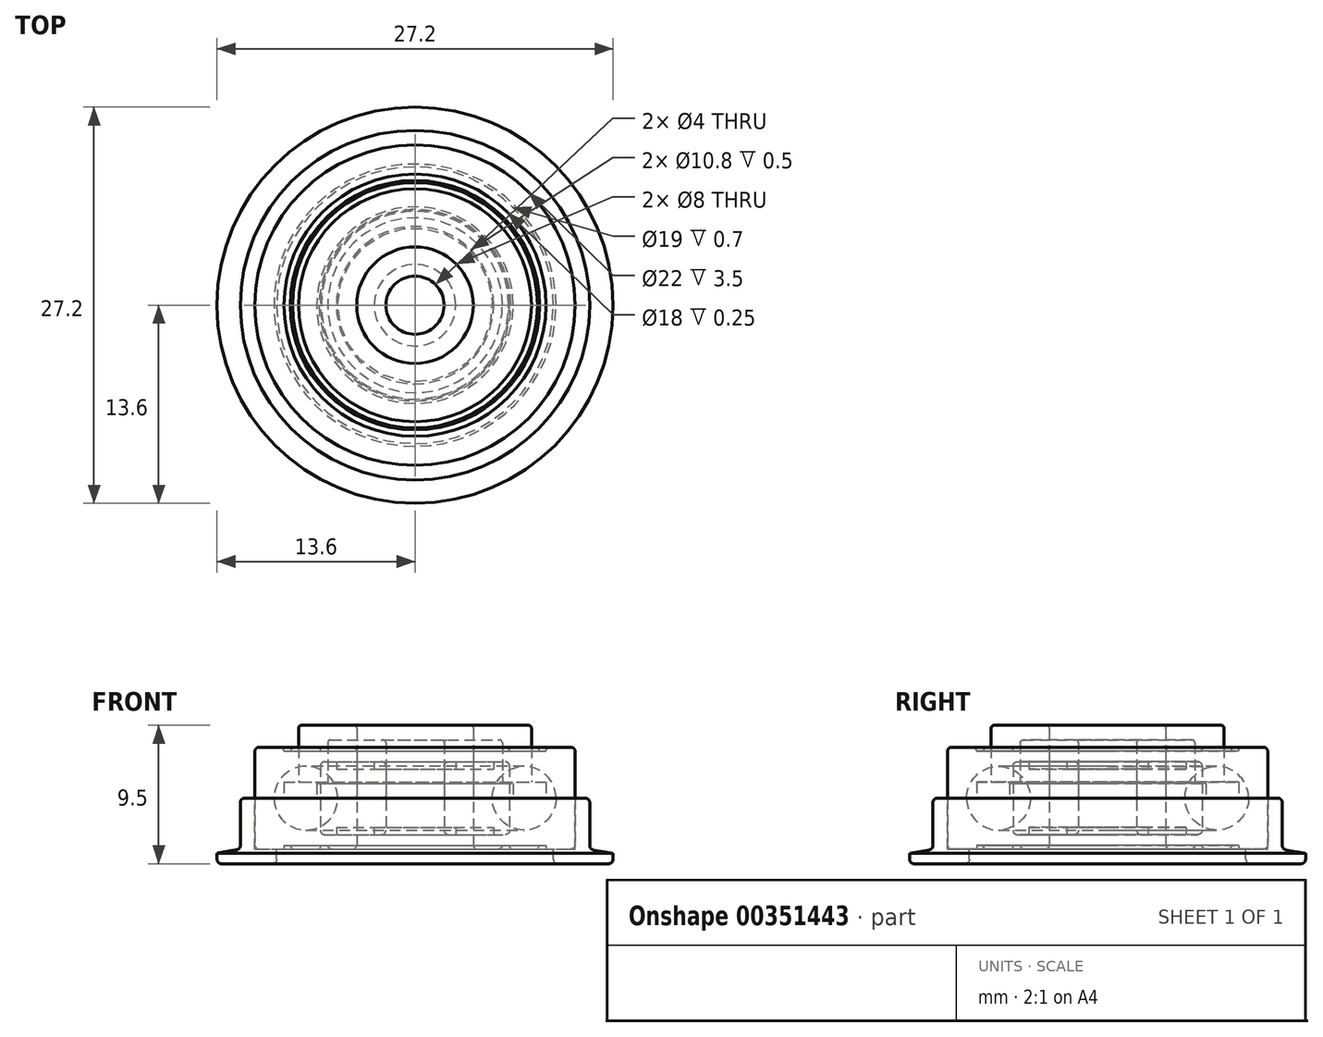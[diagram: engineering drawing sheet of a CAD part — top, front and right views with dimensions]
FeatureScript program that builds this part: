
annotation { "Feature Type Name" : "Feature", "Feature Type Description" : "" }
export const myFeature = defineFeature(function(context is Context, id is Id, definition is map)
    precondition{}
    {
        {
            var Q0;
            Q0=qCreatedBy(makeId("Front.planeOp"),FACE);
            var sketch = newSketch(context, id + "F0", { "sketchPlane" : qUnion([Q0])});
            skLineSegment(sketch, "E0", {"start": v(0, 0) * mm, "end": v(4, 0) * mm, "construction": true});
            skLineSegment(sketch, "E1", {"start": v(4, 0) * mm, "end": v(4, -3.5) * mm});
            skLineSegment(sketch, "E2", {"start": v(4, -3.5) * mm, "end": v(6, -3.5) * mm});
            skLineSegment(sketch, "E3", {"start": v(6, -3.5) * mm, "end": v(6, -3.25) * mm});
            skLineSegment(sketch, "E4", {"start": v(6, -3.25) * mm, "end": v(6.44, -3.25) * mm});
            skLineSegment(sketch, "E5", {"start": v(6.44, -3.25) * mm, "end": v(6.58, -3.5) * mm});
            skLineSegment(sketch, "E6", {"start": v(6.58, -3.5) * mm, "end": v(8.42, -3.5) * mm});
            skLineSegment(sketch, "E7", {"start": v(8.42, -3.5) * mm, "end": v(8.56, -3.25) * mm});
            skLineSegment(sketch, "E8", {"start": v(8.56, -3.25) * mm, "end": v(9, -3.25) * mm});
            skLineSegment(sketch, "E9", {"start": v(9, -3.25) * mm, "end": v(9, -3.5) * mm});
            skLineSegment(sketch, "E10", {"start": v(9, -3.5) * mm, "end": v(11, -3.5) * mm});
            skLineSegment(sketch, "E11", {"start": v(11, -3.5) * mm, "end": v(11, 0) * mm});
            skLineSegment(sketch, "E12.0.MirrorCS", {"start": v(4, 3.5) * mm, "end": v(6, 3.5) * mm});
            skLineSegment(sketch, "E12.1.MirrorCS", {"start": v(11, 3.5) * mm, "end": v(11, 0) * mm});
            skLineSegment(sketch, "E12.2.MirrorCS", {"start": v(4, 0) * mm, "end": v(4, 3.5) * mm});
            skLineSegment(sketch, "E12.3.MirrorCS", {"start": v(6, 3.25) * mm, "end": v(6.44, 3.25) * mm});
            skLineSegment(sketch, "E12.4.MirrorCS", {"start": v(9, 3.25) * mm, "end": v(9, 3.5) * mm});
            skLineSegment(sketch, "E12.5.MirrorCS", {"start": v(6.44, 3.25) * mm, "end": v(6.58, 3.5) * mm});
            skLineSegment(sketch, "E12.6.MirrorCS", {"start": v(6.58, 3.5) * mm, "end": v(8.42, 3.5) * mm});
            skLineSegment(sketch, "E12.7.MirrorCS", {"start": v(8.42, 3.5) * mm, "end": v(8.56, 3.25) * mm});
            skLineSegment(sketch, "E12.8.MirrorCS", {"start": v(9, 3.5) * mm, "end": v(11, 3.5) * mm});
            skLineSegment(sketch, "E12.9.MirrorCS", {"start": v(6, 3.5) * mm, "end": v(6, 3.25) * mm});
            skLineSegment(sketch, "E12.10.MirrorCS", {"start": v(8.56, 3.25) * mm, "end": v(9, 3.25) * mm});
            skLineSegment(sketch, "E13", {"start": v(0, 0) * mm, "end": v(0, 5.44) * mm, "construction": true});
            skLineSegment(sketch, "E14", {"start": v(0, 0) * mm, "end": v(-4, 0) * mm, "construction": true});
            skLineSegment(sketch, "E15", {"start": v(4, 0) * mm, "end": v(11, 0) * mm, "construction": true});
            skLineSegment(sketch, "E16", {"start": v(-4, 0) * mm, "end": v(-11, 0) * mm, "construction": true});
            skCircle(sketch, "E17", {"center": v(7.5, 0) * mm, "radius": 2.19 * mm});
            skSolve(sketch);
        }
        {
            var Q0;
            Q0=makeQuery(id+"F0.imprint","IMPRINT",FACE,{"disambiguationData":[TD([[makeQuery(id+"F0.imprint","IMPRINT",EDGE,{"derivedFrom":sQuery(id+"F0.wireOp",EDGE,"E2")}),1.0]])]});
            var Q1;
            Q1=sQuery(id+"F0.wireOp",EDGE,"E13");
            revolve(context, id + "F1", {"entities" : qUnion([Q0]), "axis" : qUnion([Q1]), "revolveType" : RevolveType.FULL});
        }
        {
            var Q0;
            Q0=qCreatedBy(makeId("Front.planeOp"),FACE);
            var sketch = newSketch(context, id + "F2", { "sketchPlane" : qUnion([Q0])});
            skLineSegment(sketch, "E18", {"start": v(0, 0) * mm, "end": v(0, 3.82) * mm, "construction": true});
            skLineSegment(sketch, "E19", {"start": v(0, 0) * mm, "end": v(2, 0) * mm, "construction": true});
            skLineSegment(sketch, "E20.0.MirrorCS", {"start": v(0, 0) * mm, "end": v(-2, 0) * mm, "construction": true});
            skLineSegment(sketch, "E21", {"start": v(0, 0) * mm, "end": v(6.5, 0) * mm, "construction": true});
            skLineSegment(sketch, "E22.0.MirrorCS", {"start": v(0, 0) * mm, "end": v(-6.5, 0) * mm, "construction": true});
            skLineSegment(sketch, "E23", {"start": v(6.5, 0) * mm, "end": v(6.5, 2.5) * mm});
            skLineSegment(sketch, "E24", {"start": v(2, 0) * mm, "end": v(2, 2.5) * mm});
            skLineSegment(sketch, "E25", {"start": v(2, 2.5) * mm, "end": v(2.8, 2.5) * mm});
            skLineSegment(sketch, "E26", {"start": v(2.8, 2.5) * mm, "end": v(2.8, 2) * mm});
            skLineSegment(sketch, "E27", {"start": v(2.8, 2) * mm, "end": v(5.4, 2) * mm});
            skLineSegment(sketch, "E28", {"start": v(5.4, 2) * mm, "end": v(5.4, 2.5) * mm});
            skLineSegment(sketch, "E29", {"start": v(5.4, 2.5) * mm, "end": v(6.5, 2.5) * mm});
            skLineSegment(sketch, "E30.0.MirrorCS", {"start": v(2, 0) * mm, "end": v(2, -2.5) * mm});
            skLineSegment(sketch, "E31.0.MirrorCS", {"start": v(2, -2.5) * mm, "end": v(2.8, -2.5) * mm});
            skLineSegment(sketch, "E32.0.MirrorCS", {"start": v(2.8, -2.5) * mm, "end": v(2.8, -2) * mm});
            skLineSegment(sketch, "E33.0.MirrorCS", {"start": v(2.8, -2) * mm, "end": v(5.4, -2) * mm});
            skLineSegment(sketch, "E34.0.MirrorCS", {"start": v(5.4, -2) * mm, "end": v(5.4, -2.5) * mm});
            skLineSegment(sketch, "E35.0.MirrorCS", {"start": v(5.4, -2.5) * mm, "end": v(6.5, -2.5) * mm});
            skLineSegment(sketch, "E36.0.MirrorCS", {"start": v(6.5, 0) * mm, "end": v(6.5, -2.5) * mm});
            skSolve(sketch);
        }
        {
            var Q0;
            Q0=makeQuery(id+"F2.imprint","IMPRINT",FACE,{"disambiguationData":[TD([[makeQuery(id+"F2.imprint","IMPRINT",EDGE,{"derivedFrom":sQuery(id+"F2.wireOp",EDGE,"E23")}),1.0]])]});
            var Q1;
            Q1=sQuery(id+"F2.wireOp",EDGE,"E18");
            revolve(context, id + "F3", {"entities" : qUnion([Q0]), "axis" : qUnion([Q1]), "revolveType" : RevolveType.FULL});
        }
        {
            var Q0;
            Q0=qCreatedBy(makeId("Front.planeOp"),FACE);
            var sketch = newSketch(context, id + "F4", { "sketchPlane" : qUnion([Q0])});
            skLineSegment(sketch, "E37.1", {"start": v(11, 3.5) * mm, "end": v(11, 0) * mm, "construction": true});
            skLineSegment(sketch, "E38.0", {"start": v(12, 3.5) * mm, "end": v(12, 0) * mm});
            skLineSegment(sketch, "E39", {"start": v(11, 0) * mm, "end": v(12, 0) * mm});
            skLineSegment(sketch, "E40", {"start": v(9.5, 4.5) * mm, "end": v(13.6, 4.5) * mm});
            skLineSegment(sketch, "E41", {"start": v(13.6, 4.5) * mm, "end": v(13.6, 3.78) * mm});
            skLineSegment(sketch, "E42", {"start": v(12, 3.5) * mm, "end": v(13.6, 3.78) * mm});
            skLineSegment(sketch, "E43", {"start": v(11, 3.5) * mm, "end": v(11, 0) * mm});
            skLineSegment(sketch, "E44.trimOffspring", {"start": v(9.5, 3.5) * mm, "end": v(11, 3.5) * mm});
            skLineSegment(sketch, "E45.0", {"start": v(4, 0) * mm, "end": v(4, 3.5) * mm, "construction": true});
            skLineSegment(sketch, "E46", {"start": v(9.5, 4.5) * mm, "end": v(9.5, 3.5) * mm});
            skSolve(sketch);
        }
        {
            var Q0;
            Q0=makeQuery(id+"F4.imprint","IMPRINT",FACE,{"disambiguationData":[TD([[makeQuery(id+"F4.imprint","IMPRINT",EDGE,{"derivedFrom":sQuery(id+"F4.wireOp",EDGE,"E38.0")}),-1.0]])]});
            var Q1;
            Q1=sQuery(id+"F0.wireOp",EDGE,"E13");
            revolve(context, id + "F5", {"entities" : qUnion([Q0]), "axis" : qUnion([Q1]), "revolveType" : RevolveType.FULL});
        }
        {
            var Q0;
            Q0=makeQuery(id+"F1.opRevolve","SWEPT_EDGE",EDGE,{"disambiguationData":[OSD([sQuery(id+"F0.wireOp",EDGE,"E11"),sQuery(id+"F0.wireOp",EDGE,"E12.8.MirrorCS")])]});
            var Q1;
            Q1=makeQuery(id+"F1.opRevolve","SWEPT_EDGE",EDGE,{"disambiguationData":[OSD([sQuery(id+"F0.wireOp",EDGE,"E12.0.MirrorCS"),sQuery(id+"F0.wireOp",EDGE,"E12.2.MirrorCS")])]});
            var Q2;
            Q2=makeQuery(id+"F1.opRevolve","SWEPT_EDGE",EDGE,{"disambiguationData":[OSD([sQuery(id+"F0.wireOp",EDGE,"E10"),sQuery(id+"F0.wireOp",EDGE,"E11")])]});
            var Q3;
            Q3=makeQuery(id+"F1.opRevolve","SWEPT_EDGE",EDGE,{"disambiguationData":[OSD([sQuery(id+"F0.wireOp",EDGE,"E2"),sQuery(id+"F0.wireOp",EDGE,"E12.2.MirrorCS")])]});
            var Q4;
            Q4=makeQuery(id+"F3.opRevolve","SWEPT_FACE",FACE,{"disambiguationData":[OSD([sQuery(id+"F2.wireOp",EDGE,"E23"),sQuery(id+"F2.wireOp",EDGE,"E36.0.MirrorCS")])]});
            var Q5;
            Q5=makeQuery(id+"F3.opRevolve","SWEPT_FACE",FACE,{"disambiguationData":[OSD([sQuery(id+"F2.wireOp",EDGE,"E24"),sQuery(id+"F2.wireOp",EDGE,"E30.0.MirrorCS")])]});
            var Q6;
            Q6=makeQuery(id+"F5.opRevolve","SWEPT_EDGE",EDGE,{"disambiguationData":[OSD([sQuery(id+"F4.wireOp",EDGE,"E38.0"),sQuery(id+"F4.wireOp",EDGE,"6174cbda-ea30-4576-b442-45a5408af237")])]});
            var Q7;
            Q7=makeQuery(id+"F5.opRevolve","SWEPT_EDGE",EDGE,{"disambiguationData":[OSD([sQuery(id+"F4.wireOp",EDGE,"E40"),sQuery(id+"F4.wireOp",EDGE,"E41")])]});
            var Q8;
            Q8=makeQuery(id+"F5.opRevolve","SWEPT_EDGE",EDGE,{"disambiguationData":[OSD([sQuery(id+"F4.wireOp",EDGE,"b3527501-35f9-4002-87d1-32b6eb9845c8.0"),sQuery(id+"F4.wireOp",EDGE,"E40")])]});
            fillet(context, id + "F6", {"entities" : qUnion([Q0, Q1, Q2, Q3, Q4, Q5, Q6, Q7, Q8]), "radius" : .3 * mm, "tangentPropagation" : true, "allowEdgeOverflow" : false});
        }
        {
            var Q0;
            Q0=makeQuery(id+"F5.opRevolve","SWEPT_BODY",BODY,{"disambiguationData":[OSD([sQuery(id+"F4.wireOp",EDGE,"E38.0"),sQuery(id+"F4.wireOp",EDGE,"E39"),sQuery(id+"F4.wireOp",EDGE,"E40"),sQuery(id+"F4.wireOp",EDGE,"E41"),sQuery(id+"F4.wireOp",EDGE,"E42"),sQuery(id+"F4.wireOp",EDGE,"E43"),sQuery(id+"F4.wireOp",EDGE,"E44.trimOffspring"),sQuery(id+"F4.wireOp",EDGE,"E46")])]});
            var Q1;
            Q1=sQuery(id+"F0.wireOp",EDGE,"E0");
            transform(context, id + "F7", {"entities" : qUnion([Q0]), "transformType" : TransformType.ROTATION, "transformAxis" : qUnion([Q1]), "angle" : 180 * degree, "makeCopy" : false});
        }
        {
            var Q0;
            Q0=qCreatedBy(makeId("Front.planeOp"),FACE);
            var sketch = newSketch(context, id + "F8", { "sketchPlane" : qUnion([Q0])});
            skLineSegment(sketch, "E47", {"start": v(0, 0) * mm, "end": v(0, 5) * mm, "construction": true});
            skLineSegment(sketch, "E48", {"start": v(4, 0) * mm, "end": v(4, 5) * mm});
            skLineSegment(sketch, "E49", {"start": v(4, 5) * mm, "end": v(8, 5) * mm});
            skLineSegment(sketch, "E50", {"start": v(8, 5) * mm, "end": v(8, 1.1) * mm});
            skLineSegment(sketch, "E51", {"start": v(8, 1.1) * mm, "end": v(9, 1.1) * mm});
            skLineSegment(sketch, "E52", {"start": v(9, 1.1) * mm, "end": v(9, 0) * mm});
            skLineSegment(sketch, "E53", {"start": v(9, 0) * mm, "end": v(4, 0) * mm});
            skSolve(sketch);
        }
        {
            var Q0;
            Q0=makeQuery(id+"F8.imprint","IMPRINT",FACE,{"disambiguationData":[TD([[makeQuery(id+"F8.imprint","IMPRINT",EDGE,{"derivedFrom":sQuery(id+"F8.wireOp",EDGE,"E48")}),-1.0]])]});
            var Q1;
            Q1=sQuery(id+"F8.wireOp",EDGE,"E47");
            revolve(context, id + "F9", {"entities" : qUnion([Q0]), "axis" : qUnion([Q1]), "revolveType" : RevolveType.FULL});
        }
        {
            var Q0;
            Q0=makeQuery(id+"F9.opRevolve","SWEPT_EDGE",EDGE,{"disambiguationData":[OSD([sQuery(id+"F8.wireOp",EDGE,"E48"),sQuery(id+"F8.wireOp",EDGE,"E53")])]});
            var Q1;
            Q1=makeQuery(id+"F9.opRevolve","SWEPT_FACE",FACE,{"disambiguationData":[OSD([sQuery(id+"F8.wireOp",EDGE,"E49")])]});
            fillet(context, id + "F10", {"entities" : qUnion([Q0, Q1]), "radius" : 0.2 * mm, "tangentPropagation" : true, "allowEdgeOverflow" : false});
        }
        {
            var Q0;
            Q0=qCreatedBy(makeId("Front.planeOp"),FACE);
            var sketch = newSketch(context, id + "F11", { "sketchPlane" : qUnion([Q0])});
            skLineSegment(sketch, "E54", {"start": v(0, 0) * mm, "end": v(0, 4) * mm, "construction": true});
            skLineSegment(sketch, "E55", {"start": v(2, 0) * mm, "end": v(2, 4) * mm});
            skLineSegment(sketch, "E56", {"start": v(2, 4) * mm, "end": v(6, 4) * mm});
            skLineSegment(sketch, "E57", {"start": v(6, 4) * mm, "end": v(6, 1) * mm});
            skLineSegment(sketch, "E58", {"start": v(6, 1) * mm, "end": v(6.75, 1) * mm});
            skLineSegment(sketch, "E59", {"start": v(6.75, 1) * mm, "end": v(6.75, 0) * mm});
            skLineSegment(sketch, "E60", {"start": v(6.75, 0) * mm, "end": v(2, 0) * mm});
            skSolve(sketch);
        }
        {
            var Q0;
            Q0=qSketchRegion(id+"F11",true);
            var Q1;
            Q1=sQuery(id+"F11.wireOp",EDGE,"E54");
            revolve(context, id + "F12", {"entities" : qUnion([Q0]), "axis" : qUnion([Q1]), "revolveType" : RevolveType.FULL});
        }
        {
            var Q0;
            Q0=makeQuery(id+"F12.opRevolve","SWEPT_FACE",FACE,{"disambiguationData":[OSD([sQuery(id+"F11.wireOp",EDGE,"E56")])]});
            var Q1;
            Q1=makeQuery(id+"F12.opRevolve","SWEPT_EDGE",EDGE,{"disambiguationData":[OSD([sQuery(id+"F11.wireOp",EDGE,"E55"),sQuery(id+"F11.wireOp",EDGE,"E60")])]});
            fillet(context, id + "F13", {"entities" : qUnion([Q0, Q1]), "radius" : .2 * mm, "tangentPropagation" : true, "allowEdgeOverflow" : false});
        }
    });
